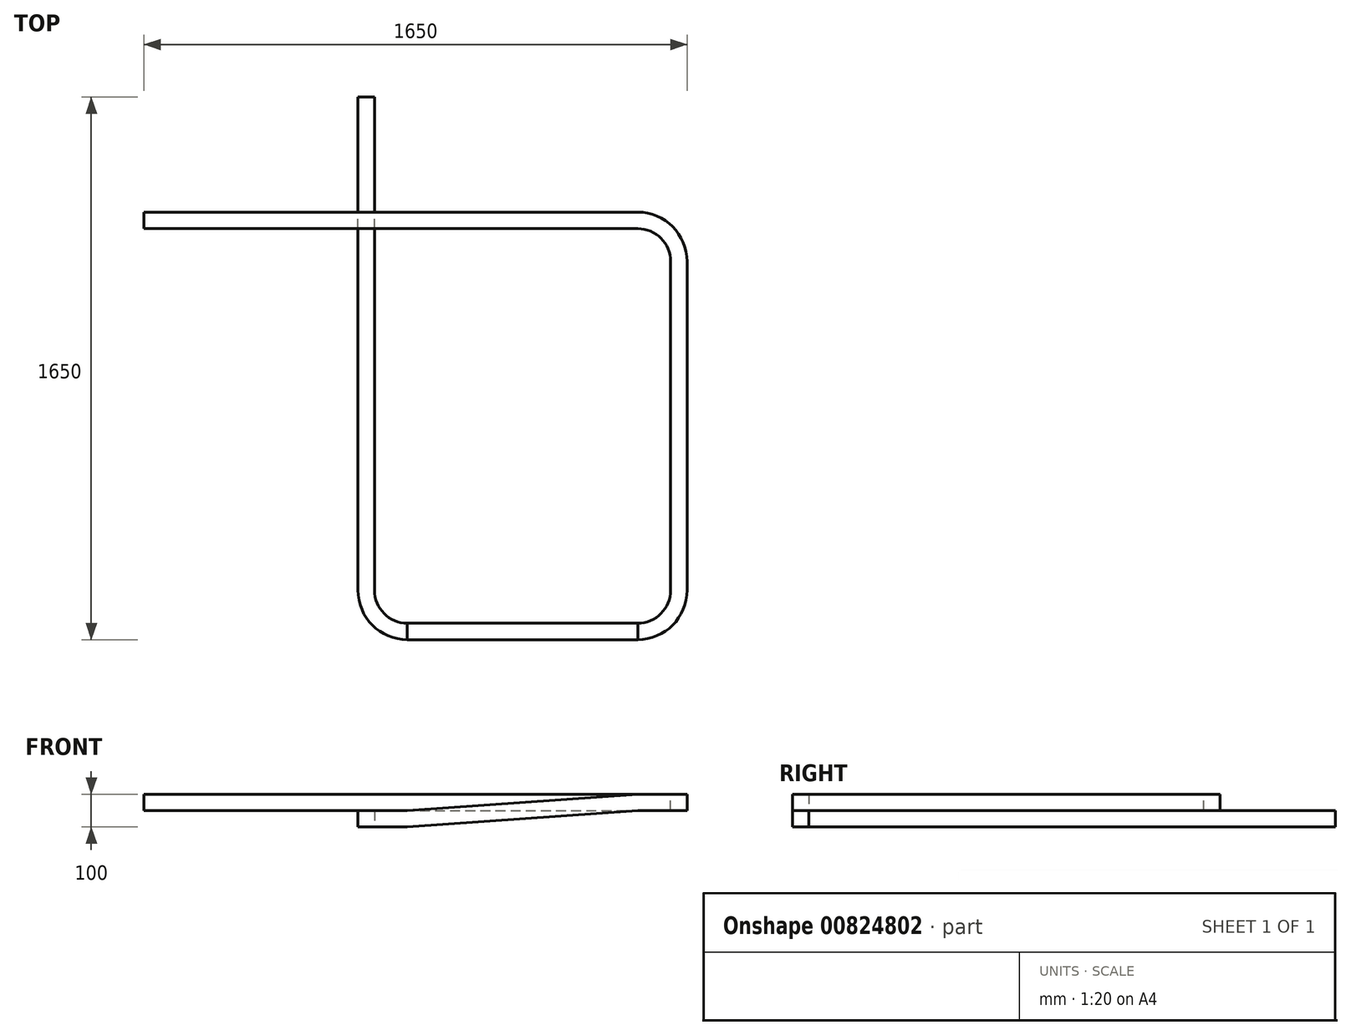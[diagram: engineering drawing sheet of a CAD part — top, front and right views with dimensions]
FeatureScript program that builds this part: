
annotation { "Feature Type Name" : "Feature", "Feature Type Description" : "" }
export const myFeature = defineFeature(function(context is Context, id is Id, definition is map)
    precondition{}
    {
        {
            var Q0;
            Q0=qCreatedBy(makeId("Front.planeOp"),FACE);
            var sketch = newSketch(context, id + "F0", { "sketchPlane" : qUnion([Q0])});
            skLineSegment(sketch, "E0.bottom", {"start": v(450, 0) * mm, "end": v(500, 0) * mm});
            skLineSegment(sketch, "E0.top", {"start": v(450, 50) * mm, "end": v(500, 50) * mm});
            skLineSegment(sketch, "E0.left", {"start": v(450, 0) * mm, "end": v(450, 50) * mm});
            skLineSegment(sketch, "E0.right", {"start": v(500, 0) * mm, "end": v(500, 50) * mm});
            skLineSegment(sketch, "E1.bottom", {"start": v(-450, 0) * mm, "end": v(-500, 0) * mm});
            skLineSegment(sketch, "E1.top", {"start": v(-450, -50) * mm, "end": v(-500, -50) * mm});
            skLineSegment(sketch, "E1.left", {"start": v(-450, 0) * mm, "end": v(-450, -50) * mm});
            skLineSegment(sketch, "E1.right", {"start": v(-500, 0) * mm, "end": v(-500, -50) * mm});
            skSolve(sketch);
        }
        {
            var Q0;
            Q0 = qSketchRegion(id + "F0", true);
            extrude(context, id + "F1", {"entities" : qUnion([Q0]), "endBound" : BoundingType.SYMMETRIC, "depth" : 1000 * mm, "offsetDistance" : 25 * mm});
        }
        {
            var Q0;
            Q0=qCreatedBy(makeId("Front.planeOp"),FACE);
            cPlane(context, id + "F2", {"entities" : qUnion([Q0]), "cplaneType" : CPlaneType.OFFSET, "offset" : 500 * mm, "width" : 150 * mm, "height" : 150 * mm});
        }
        {
            var Q0;
            Q0=qCreatedBy(id+"F2.planeOp",FACE);
            var sketch = newSketch(context, id + "F3", { "sketchPlane" : qUnion([Q0])});
            skLineSegment(sketch, "E2.bottom", {"start": v(-500, 0) * mm, "end": v(-450, 0) * mm});
            skLineSegment(sketch, "E2.top", {"start": v(-500, -50) * mm, "end": v(-450, -50) * mm});
            skLineSegment(sketch, "E2.left", {"start": v(-500, 0) * mm, "end": v(-500, -50) * mm});
            skLineSegment(sketch, "E2.right", {"start": v(-450, 0) * mm, "end": v(-450, -50) * mm});
            skLineSegment(sketch, "E3.bottom", {"start": v(450, 50) * mm, "end": v(500, 50) * mm});
            skLineSegment(sketch, "E3.top", {"start": v(450, 0) * mm, "end": v(500, 0) * mm});
            skLineSegment(sketch, "E3.left", {"start": v(450, 50) * mm, "end": v(450, 0) * mm});
            skLineSegment(sketch, "E3.right", {"start": v(500, 50) * mm, "end": v(500, 0) * mm});
            skLineSegment(sketch, "E4", {"start": v(-350, 53.8) * mm, "end": v(-350, -119.1) * mm});
            skLineSegment(sketch, "E5", {"start": v(350, 85.7) * mm, "end": v(350, -93.13) * mm});
            skSolve(sketch);
        }
        {
            var Q0;
            Q0=makeQuery(id+"F3.imprint","IMPRINT",FACE,{"disambiguationData":[TD([[makeQuery(id+"F3.imprint","IMPRINT",EDGE,{"derivedFrom":sQuery(id+"F3.wireOp",EDGE,"E2.bottom")}),-1.0]])]});
            var Q1;
            Q1=sQuery(id+"F3.wireOp",EDGE,"E4");
            revolve(context, id + "F4", {"operationType" : NewBodyOperationType.ADD, "surfaceOperationType" : NewSurfaceOperationType.NEW, "entities" : qUnion([Q0]), "axis" : qUnion([Q1]), "revolveType" : RevolveType.ONE_DIRECTION, "oppositeDirection" : true, "angle" : 90 * degree});
        }
        {
            var Q0;
            Q0=makeQuery(id+"F3.imprint","IMPRINT",FACE,{"disambiguationData":[TD([[makeQuery(id+"F3.imprint","IMPRINT",EDGE,{"derivedFrom":sQuery(id+"F3.wireOp",EDGE,"E3.bottom")}),-1.0]])]});
            var Q1;
            Q1=sQuery(id+"F3.wireOp",EDGE,"E5");
            revolve(context, id + "F5", {"operationType" : NewBodyOperationType.ADD, "surfaceOperationType" : NewSurfaceOperationType.NEW, "entities" : qUnion([Q0]), "axis" : qUnion([Q1]), "revolveType" : RevolveType.ONE_DIRECTION, "angle" : 90 * degree});
        }
        {
            var Q0;
            Q0=makeQuery(id+"F4.opRevolve","CAP_FACE",FACE,{"disambiguationData":[OSD([sQuery(id+"F3.wireOp",EDGE,"E2.bottom"),sQuery(id+"F3.wireOp",EDGE,"E2.top"),sQuery(id+"F3.wireOp",EDGE,"E2.left"),sQuery(id+"F3.wireOp",EDGE,"E2.right")])],"isStart":false});
            var Q1;
            Q1=makeQuery(id+"F5.opRevolve","CAP_FACE",FACE,{"disambiguationData":[OSD([sQuery(id+"F3.wireOp",EDGE,"E3.bottom"),sQuery(id+"F3.wireOp",EDGE,"E3.top"),sQuery(id+"F3.wireOp",EDGE,"E3.left"),sQuery(id+"F3.wireOp",EDGE,"E3.right")])],"isStart":false});
            loft(context, id + "F6", {"operationType" : NewBodyOperationType.ADD, "sheetProfilesArray" : [{ "sheetProfileEntities" : qUnion([Q0]) }, { "sheetProfileEntities" : qUnion([Q1]) }]});
        }
        {
            var Q0;
            Q0=makeQuery(id+"F1.opExtrude","CAP_FACE",FACE,{"disambiguationData":[OSD([sQuery(id+"F0.wireOp",EDGE,"E1.bottom"),sQuery(id+"F0.wireOp",EDGE,"E1.top"),sQuery(id+"F0.wireOp",EDGE,"E1.left"),sQuery(id+"F0.wireOp",EDGE,"E1.right")])],"isStart":true});
            extrude(context, id + "F7", {"entities" : qUnion([Q0]), "operationType" : NewBodyOperationType.ADD, "depth" : 500 * mm, "offsetDistance" : 25 * mm});
        }
        {
            var Q0;
            Q0=makeQuery(id+"F1.opExtrude","CAP_FACE",FACE,{"disambiguationData":[OSD([sQuery(id+"F0.wireOp",EDGE,"E0.bottom"),sQuery(id+"F0.wireOp",EDGE,"E0.top"),sQuery(id+"F0.wireOp",EDGE,"E0.left"),sQuery(id+"F0.wireOp",EDGE,"E0.right")])],"isStart":true});
            var sketch = newSketch(context, id + "F8", { "sketchPlane" : qUnion([Q0])});
            skLineSegment(sketch, "E6.bottom", {"start": v(-500, 50) * mm, "end": v(-450, 50) * mm});
            skLineSegment(sketch, "E6.top", {"start": v(-500, 0) * mm, "end": v(-450, 0) * mm});
            skLineSegment(sketch, "E6.left", {"start": v(-500, 50) * mm, "end": v(-500, 0) * mm});
            skLineSegment(sketch, "E6.right", {"start": v(-450, 50) * mm, "end": v(-450, 0) * mm});
            skLineSegment(sketch, "E7", {"start": v(-350, 86.82) * mm, "end": v(-350, -89.79) * mm});
            skSolve(sketch);
        }
        {
            var Q0;
            Q0=makeQuery(id+"F8.imprint","IMPRINT",FACE,{"disambiguationData":[TD([[makeQuery(id+"F8.imprint","IMPRINT",EDGE,{"derivedFrom":sQuery(id+"F8.wireOp",EDGE,"E6.bottom")}),1.0]])]});
            var Q1;
            Q1=sQuery(id+"F8.wireOp",EDGE,"E7");
            revolve(context, id + "F9", {"operationType" : NewBodyOperationType.ADD, "surfaceOperationType" : NewSurfaceOperationType.NEW, "entities" : qUnion([Q0]), "axis" : qUnion([Q1]), "revolveType" : RevolveType.ONE_DIRECTION, "oppositeDirection" : true, "angle" : 90 * degree});
        }
        {
            var Q0;
            Q0=makeQuery(id+"F9.opRevolve","CAP_FACE",FACE,{"disambiguationData":[OSD([sQuery(id+"F8.wireOp",EDGE,"E6.bottom"),sQuery(id+"F8.wireOp",EDGE,"E6.top"),sQuery(id+"F8.wireOp",EDGE,"E6.left"),sQuery(id+"F8.wireOp",EDGE,"E6.right")])],"isStart":false});
            extrude(context, id + "F10", {"entities" : qUnion([Q0]), "operationType" : NewBodyOperationType.ADD, "depth" : 1500 * mm, "offsetDistance" : 25 * mm});
        }
    });
